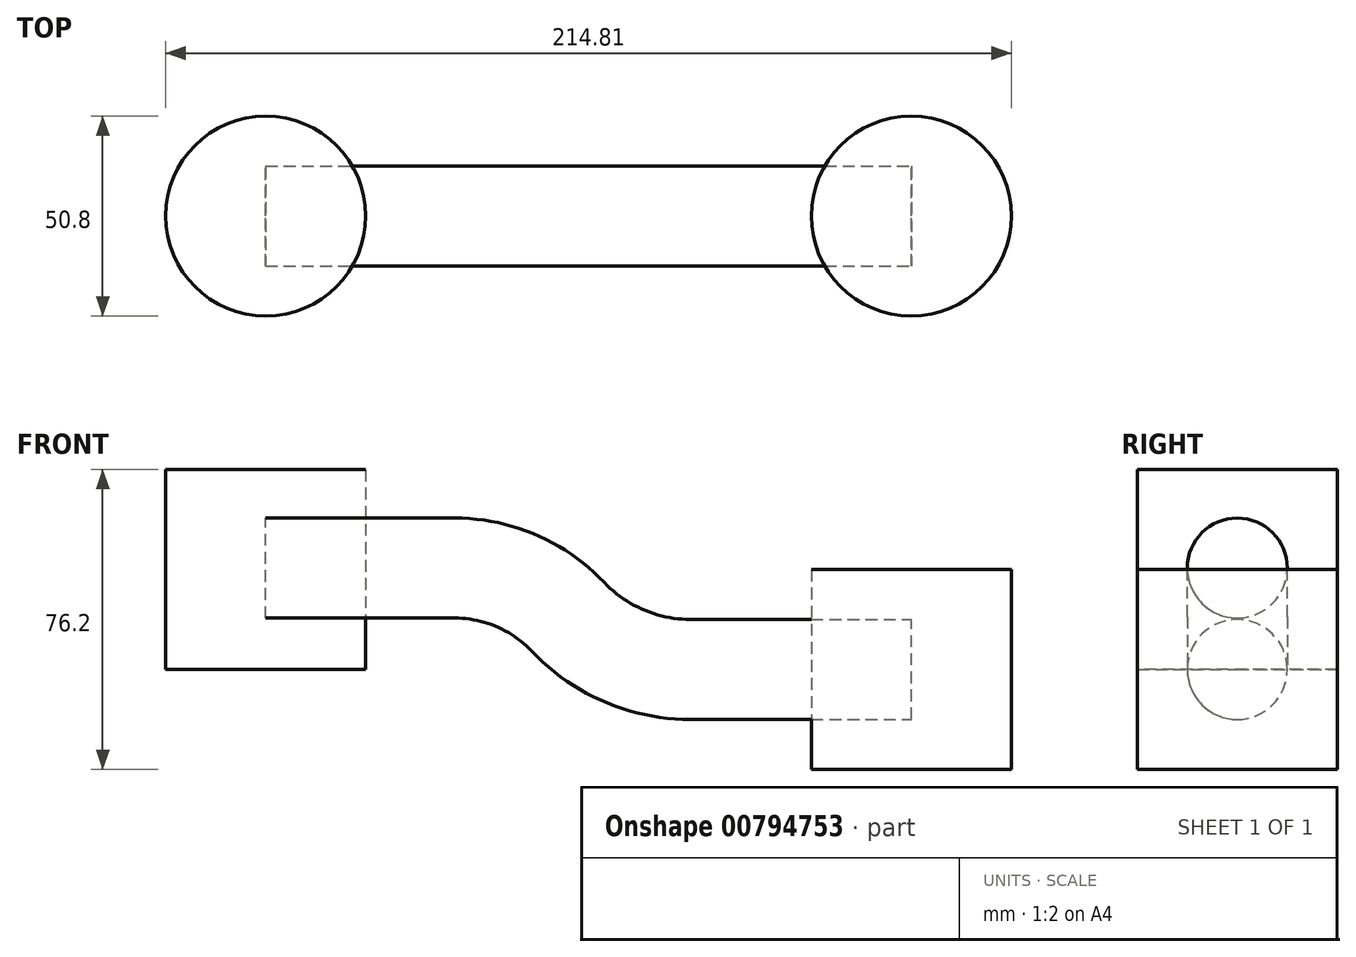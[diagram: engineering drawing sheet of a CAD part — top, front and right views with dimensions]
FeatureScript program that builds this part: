
annotation { "Feature Type Name" : "Feature", "Feature Type Description" : "" }
export const myFeature = defineFeature(function(context is Context, id is Id, definition is map)
    precondition{}
    {
        {
            var Q0;
            Q0=qCreatedBy(makeId("Top.planeOp"),FACE);
            var sketch = newSketch(context, id + "F0", { "sketchPlane" : qUnion([Q0])});
            skCircle(sketch, "E0", {"center": v(0, 0) * mm, "radius": 25.4 * mm});
            skCircle(sketch, "E1", {"center": v(164, 0) * mm, "radius": 25.4 * mm});
            skSolve(sketch);
        }
        {
            var Q0;
            Q0=makeQuery(id+"F0.imprint","IMPRINT",FACE,{"disambiguationData":[TD([[makeQuery(id+"F0.imprint","IMPRINT",EDGE,{"derivedFrom":sQuery(id+"F0.wireOp",EDGE,"E0")}),1.0]])]});
            extrude(context, id + "F1", {"entities" : qUnion([Q0]), "depth" : 50.8 * mm, "offsetDistance" : 25.4 * mm});
        }
        {
            var Q0;
            Q0=makeQuery(id+"F0.imprint","IMPRINT",FACE,{"disambiguationData":[TD([[makeQuery(id+"F0.imprint","IMPRINT",EDGE,{"derivedFrom":sQuery(id+"F0.wireOp",EDGE,"E1")}),1.0]])]});
            extrude(context, id + "F2", {"entities" : qUnion([Q0]), "endBound" : BoundingType.SYMMETRIC, "depth" : 50.8 * mm, "offsetDistance" : 25.4 * mm});
        }
        {
            var Q0;
            Q0=qCreatedBy(makeId("Front.planeOp"),FACE);
            var sketch = newSketch(context, id + "F3", { "sketchPlane" : qUnion([Q0])});
            skLineSegment(sketch, "E2", {"start": v(0, 25.77) * mm, "end": v(48.03, 25.77) * mm});
            skArc(sketch, "E3", {"start": v(48.03, 25.77) * mm, "mid": v(63.68, 22.54) * mm, "end": v(76.78, 13.39) * mm});
            skArc(sketch, "E4", {"start": v(76.78, 13.39) * mm, "mid": v(90.95, 3.49) * mm, "end": v(107.87, 0) * mm});
            skLineSegment(sketch, "E5", {"start": v(107.87, 0) * mm, "end": v(164, 0) * mm});
            skSolve(sketch);
        }
        {
            var Q0;
            Q0=qCreatedBy(makeId("Right.planeOp"),FACE);
            var sketch = newSketch(context, id + "F4", { "sketchPlane" : qUnion([Q0])});
            skCircle(sketch, "E6", {"center": v(0, 25.77) * mm, "radius": 12.7 * mm});
            skSolve(sketch);
        }
        {
            var Q0;
            Q0 = qSketchRegion(id + "F4", true);
            var Q1;
            Q1 = qConstructionFilter(qBodyType(qCreatedBy(id + "F3" ,EDGE), BodyType.WIRE), ConstructionObject.NO);
            sweep(context, id + "F5", {"profiles" : qUnion([Q0]), "path" : qUnion([Q1])});
        }
    });
